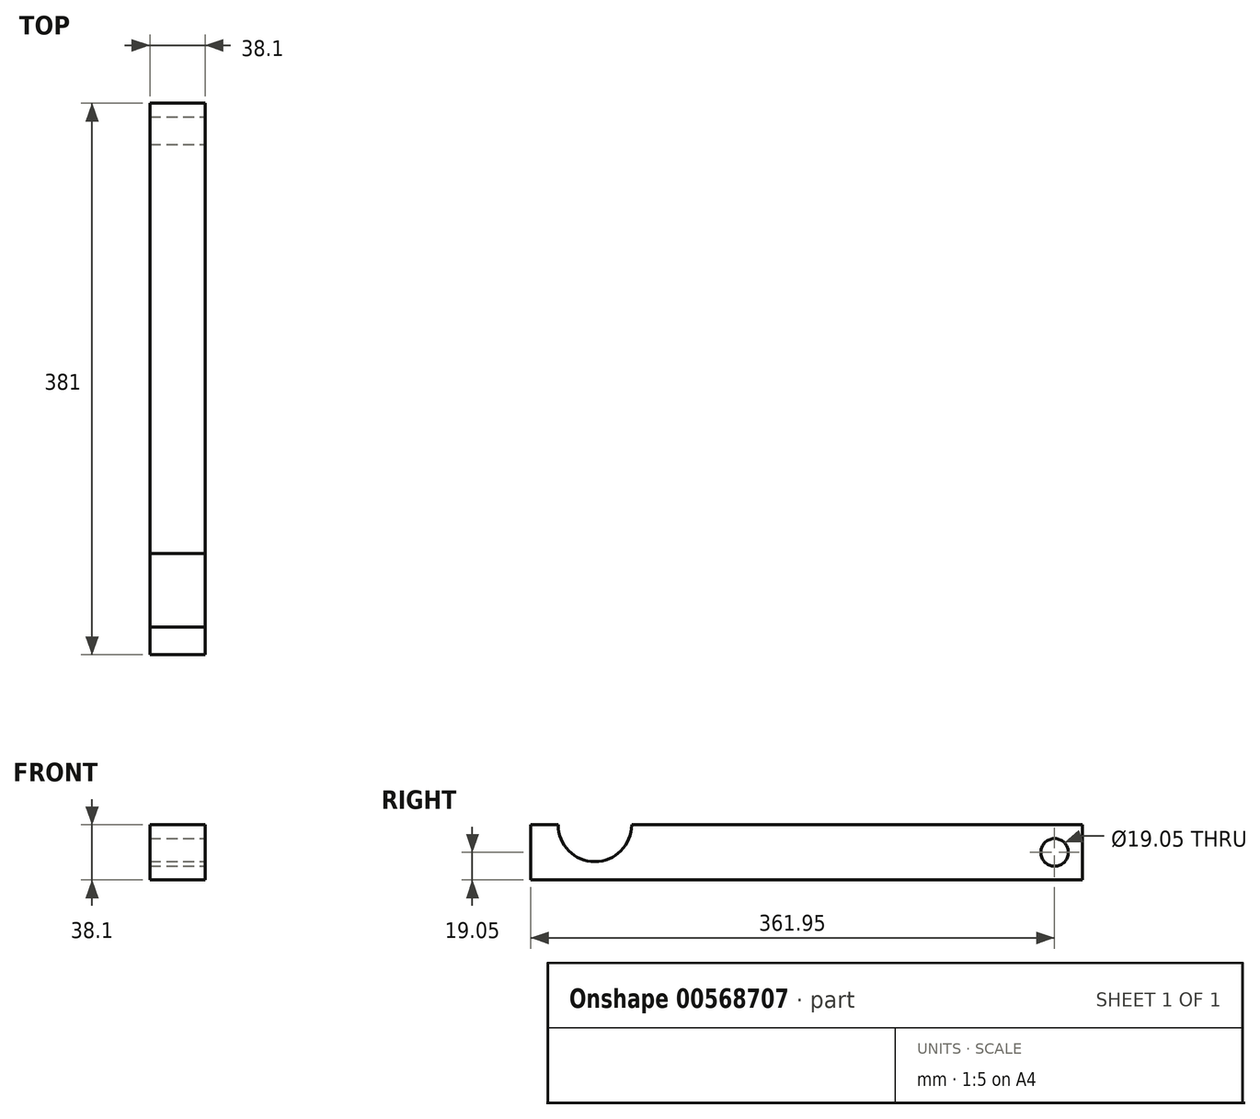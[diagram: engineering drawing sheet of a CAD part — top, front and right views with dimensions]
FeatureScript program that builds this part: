
annotation { "Feature Type Name" : "Feature", "Feature Type Description" : "" }
export const myFeature = defineFeature(function(context is Context, id is Id, definition is map)
    precondition{}
    {
        {
            var Q0;
            Q0=qCreatedBy(makeId("Front.planeOp"),FACE);
            var sketch = newSketch(context, id + "F0", { "sketchPlane" : qUnion([Q0])});
            skLineSegment(sketch, "E0.bottom", {"start": v(19.05, 19.05) * mm, "end": v(-19.05, 19.05) * mm});
            skLineSegment(sketch, "E0.top", {"start": v(19.05, -19.05) * mm, "end": v(-19.05, -19.05) * mm});
            skLineSegment(sketch, "E0.left", {"start": v(19.05, 19.05) * mm, "end": v(19.05, -19.05) * mm});
            skLineSegment(sketch, "E0.right", {"start": v(-19.05, 19.05) * mm, "end": v(-19.05, -19.05) * mm});
            skPoint(sketch, "E0.middle", {"position": v(0, 0) * mm});
            skSolve(sketch);
        }
        {
            var Q0;
            Q0 = qSketchRegion(id + "F0", true);
            extrude(context, id + "F1", {"entities" : qUnion([Q0]), "endBound" : BoundingType.SYMMETRIC, "depth" : 381 * mm, "offsetDistance" : 25.4 * mm});
        }
        {
            var Q0;
            Q0=makeQuery(id+"F1.opExtrude","SWEPT_FACE",FACE,{"disambiguationData":[OSD([sQuery(id+"F0.wireOp",EDGE,"E0.left")])]});
            var sketch = newSketch(context, id + "F2", { "sketchPlane" : qUnion([Q0])});
            skLineSegment(sketch, "E1.0", {"start": v(-190.5, 19.05) * mm, "end": v(190.5, 19.05) * mm, "construction": true});
            skLineSegment(sketch, "E1.1", {"start": v(-190.5, -19.05) * mm, "end": v(190.5, -19.05) * mm, "construction": true});
            skLineSegment(sketch, "E2.0", {"start": v(-190.5, 19.05) * mm, "end": v(-190.5, -19.05) * mm, "construction": true});
            skCircle(sketch, "E3", {"center": v(-146.05, 19.05) * mm, "radius": 25.4 * mm});
            skLineSegment(sketch, "E4.3", {"start": v(190.5, 19.05) * mm, "end": v(190.5, -19.05) * mm, "construction": true});
            skSolve(sketch);
        }
        {
            var Q0;
            Q0 = qSketchRegion(id + "F2", true);
            extrude(context, id + "F3", {"entities" : qUnion([Q0]), "operationType" : NewBodyOperationType.REMOVE, "endBound" : BoundingType.THROUGH_ALL, "oppositeDirection" : true, "depth" : 25.4 * mm, "offsetDistance" : 25.4 * mm});
        }
        {
            var Q0;
            Q0=makeQuery(id+"F1.opExtrude","SWEPT_FACE",FACE,{"disambiguationData":[OSD([sQuery(id+"F0.wireOp",EDGE,"E0.left")])]});
            var sketch = newSketch(context, id + "F4", { "sketchPlane" : qUnion([Q0])});
            skLineSegment(sketch, "E5.0", {"start": v(-190.5, -19.05) * mm, "end": v(190.5, -19.05) * mm, "construction": true});
            skLineSegment(sketch, "E5.1", {"start": v(190.5, 19.05) * mm, "end": v(190.5, -19.05) * mm, "construction": true});
            skLineSegment(sketch, "E5.2", {"start": v(-120.65, 19.05) * mm, "end": v(190.5, 19.05) * mm, "construction": true});
            skLineSegment(sketch, "E6", {"start": v(152.4, 0) * mm, "end": v(190.5, 0) * mm, "construction": true});
            skLineSegment(sketch, "E7", {"start": v(152.4, -19.05) * mm, "end": v(152.4, 19.05) * mm, "construction": true});
            skCircle(sketch, "E8", {"center": v(171.45, 0) * mm, "radius": 9.53 * mm});
            skSolve(sketch);
        }
        {
            var Q0;
            Q0 = qSketchRegion(id + "F4", true);
            extrude(context, id + "F5", {"entities" : qUnion([Q0]), "operationType" : NewBodyOperationType.REMOVE, "endBound" : BoundingType.THROUGH_ALL, "oppositeDirection" : true, "depth" : 25.4 * mm, "offsetDistance" : 25.4 * mm});
        }
    });
